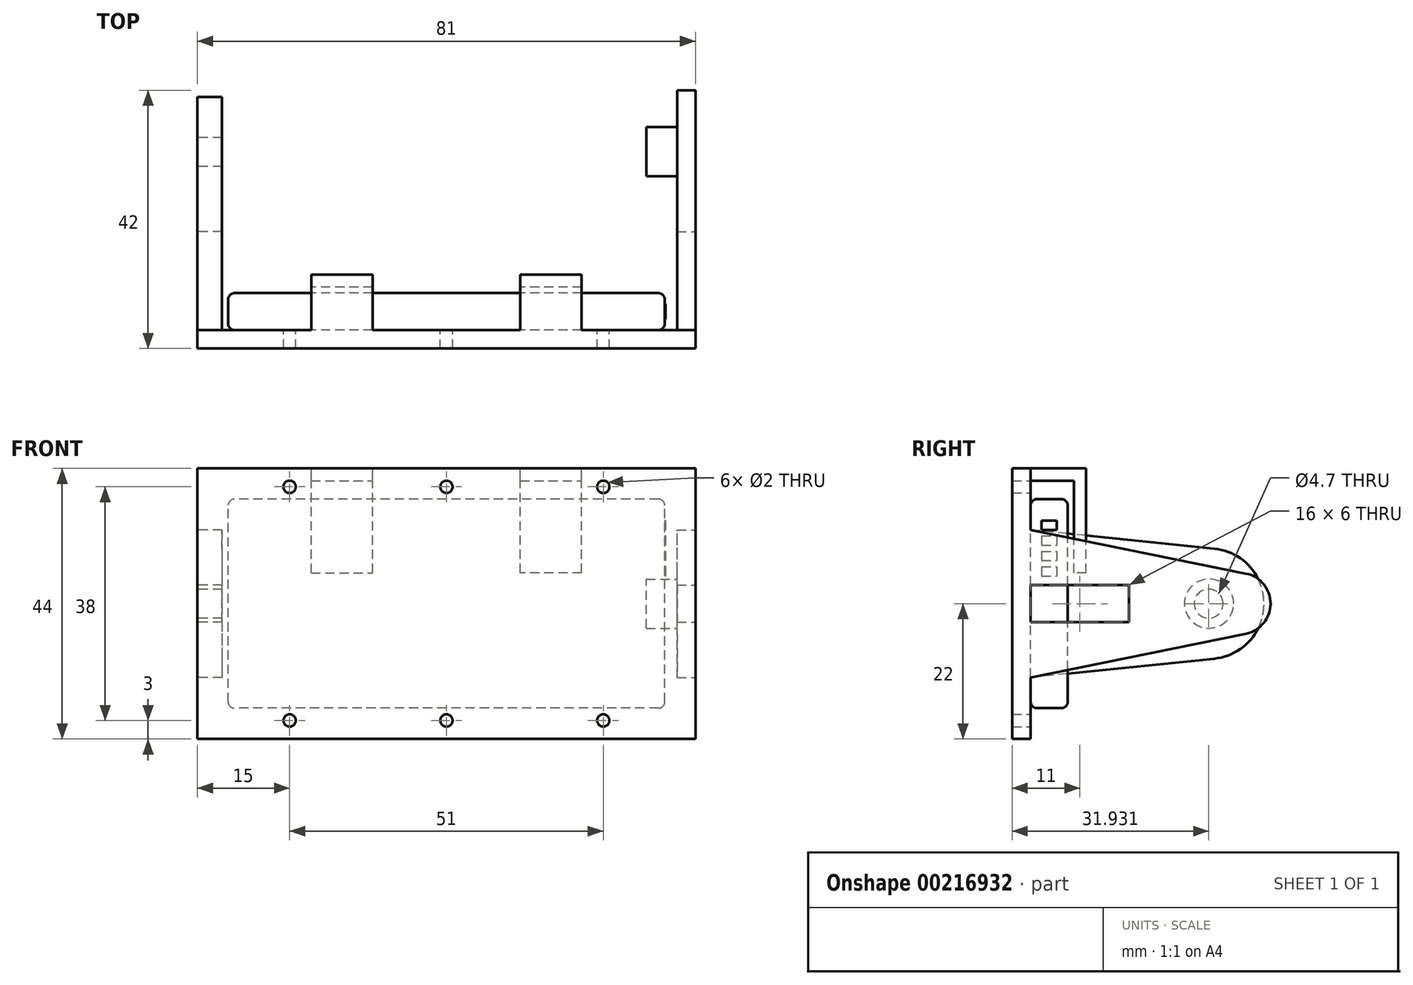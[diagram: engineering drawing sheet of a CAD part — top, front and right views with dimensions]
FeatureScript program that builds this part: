
annotation { "Feature Type Name" : "Feature", "Feature Type Description" : "" }
export const myFeature = defineFeature(function(context is Context, id is Id, definition is map)
    precondition{}
    {
        {
            var Q0;
            Q0=qCreatedBy(makeId("Front.planeOp"),FACE);
            var sketch = newSketch(context, id + "F0", { "sketchPlane" : qUnion([Q0])});
            skLineSegment(sketch, "E0.bottom", {"start": v(35.5, -17) * mm, "end": v(-35.5, -17) * mm});
            skLineSegment(sketch, "E0.top", {"start": v(35.5, 17) * mm, "end": v(-35.5, 17) * mm});
            skLineSegment(sketch, "E0.left", {"start": v(35.5, -17) * mm, "end": v(35.5, 17) * mm});
            skLineSegment(sketch, "E0.right", {"start": v(-35.5, -17) * mm, "end": v(-35.5, 17) * mm});
            skPoint(sketch, "E0.middle", {"position": v(0, 0) * mm});
            skSolve(sketch);
        }
        {
            var Q0;
            Q0 = qSketchRegion(id + "F0", true);
            extrude(context, id + "F1", {"entities" : qUnion([Q0]), "endBound" : BoundingType.SYMMETRIC, "depth" : 6 * mm});
        }
        {
            var Q0;
            Q0=makeQuery(id+"F1.opExtrude","CAP_EDGE",EDGE,{"disambiguationData":[OSD([sQuery(id+"F0.wireOp",EDGE,"E0.top")])],"isStart":false});
            var Q1;
            Q1=makeQuery(id+"F1.opExtrude","CAP_EDGE",EDGE,{"disambiguationData":[OSD([sQuery(id+"F0.wireOp",EDGE,"E0.top")])],"isStart":true});
            var Q2;
            Q2=makeQuery(id+"F1.opExtrude","CAP_EDGE",EDGE,{"disambiguationData":[OSD([sQuery(id+"F0.wireOp",EDGE,"E0.left")])],"isStart":false});
            var Q3;
            Q3=makeQuery(id+"F1.opExtrude","CAP_EDGE",EDGE,{"disambiguationData":[OSD([sQuery(id+"F0.wireOp",EDGE,"E0.left")])],"isStart":true});
            var Q4;
            Q4=makeQuery(id+"F1.opExtrude","CAP_EDGE",EDGE,{"disambiguationData":[OSD([sQuery(id+"F0.wireOp",EDGE,"E0.bottom")])],"isStart":false});
            var Q5;
            Q5=makeQuery(id+"F1.opExtrude","SWEPT_EDGE",EDGE,{"disambiguationData":[OSD([sQuery(id+"F0.wireOp",EDGE,"E0.bottom"),sQuery(id+"F0.wireOp",EDGE,"E0.left")])]});
            var Q6;
            Q6=makeQuery(id+"F1.opExtrude","SWEPT_EDGE",EDGE,{"disambiguationData":[OSD([sQuery(id+"F0.wireOp",EDGE,"E0.top"),sQuery(id+"F0.wireOp",EDGE,"E0.right")])]});
            var Q7;
            Q7=makeQuery(id+"F1.opExtrude","CAP_EDGE",EDGE,{"disambiguationData":[OSD([sQuery(id+"F0.wireOp",EDGE,"E0.right")])],"isStart":false});
            var Q8;
            Q8=makeQuery(id+"F1.opExtrude","CAP_EDGE",EDGE,{"disambiguationData":[OSD([sQuery(id+"F0.wireOp",EDGE,"E0.right")])],"isStart":true});
            var Q9;
            Q9=makeQuery(id+"F1.opExtrude","CAP_EDGE",EDGE,{"disambiguationData":[OSD([sQuery(id+"F0.wireOp",EDGE,"E0.bottom")])],"isStart":true});
            var Q10;
            Q10=makeQuery(id+"F1.opExtrude","SWEPT_EDGE",EDGE,{"disambiguationData":[OSD([sQuery(id+"F0.wireOp",EDGE,"E0.bottom"),sQuery(id+"F0.wireOp",EDGE,"E0.right")])]});
            var Q11;
            Q11=makeQuery(id+"F1.opExtrude","SWEPT_EDGE",EDGE,{"disambiguationData":[OSD([sQuery(id+"F0.wireOp",EDGE,"E0.top"),sQuery(id+"F0.wireOp",EDGE,"E0.left")])]});
            fillet(context, id + "F2", {"entities" : qUnion([Q0, Q1, Q2, Q3, Q4, Q5, Q6, Q7, Q8, Q9, Q10, Q11]), "radius" : 1 * mm, "tangentPropagation" : true, "allowEdgeOverflow" : false});
        }
        {
            var Q0;
            Q0=makeQuery(id+"F1.opExtrude","SWEPT_FACE",FACE,{"disambiguationData":[OSD([sQuery(id+"F0.wireOp",EDGE,"E0.left")])]});
            var sketch = newSketch(context, id + "F3", { "sketchPlane" : qUnion([Q0])});
            skLineSegment(sketch, "E1.bottom", {"start": v(-1.25, 13.5) * mm, "end": v(1.25, 13.5) * mm});
            skLineSegment(sketch, "E1.top", {"start": v(-1.25, 12) * mm, "end": v(1.25, 12) * mm});
            skLineSegment(sketch, "E1.left", {"start": v(-1.25, 13.5) * mm, "end": v(-1.25, 12) * mm});
            skLineSegment(sketch, "E1.right", {"start": v(1.25, 13.5) * mm, "end": v(1.25, 12) * mm});
            skLineSegment(sketch, "E2.bottom", {"start": v(-1.25, 11) * mm, "end": v(1.25, 11) * mm});
            skLineSegment(sketch, "E2.top", {"start": v(-1.25, 9.5) * mm, "end": v(1.25, 9.5) * mm});
            skLineSegment(sketch, "E2.left", {"start": v(-1.25, 11) * mm, "end": v(-1.25, 9.5) * mm});
            skLineSegment(sketch, "E2.right", {"start": v(1.25, 11) * mm, "end": v(1.25, 9.5) * mm});
            skLineSegment(sketch, "E3.bottom", {"start": v(-1.25, 8.5) * mm, "end": v(1.25, 8.5) * mm});
            skLineSegment(sketch, "E3.top", {"start": v(-1.25, 7) * mm, "end": v(1.25, 7) * mm});
            skLineSegment(sketch, "E3.left", {"start": v(-1.25, 8.5) * mm, "end": v(-1.25, 7) * mm});
            skLineSegment(sketch, "E3.right", {"start": v(1.25, 8.5) * mm, "end": v(1.25, 7) * mm});
            skLineSegment(sketch, "E4.bottom", {"start": v(-1.25, 6) * mm, "end": v(1.25, 6) * mm});
            skLineSegment(sketch, "E4.top", {"start": v(-1.25, 4.5) * mm, "end": v(1.25, 4.5) * mm});
            skLineSegment(sketch, "E4.left", {"start": v(-1.25, 6) * mm, "end": v(-1.25, 4.5) * mm});
            skLineSegment(sketch, "E4.right", {"start": v(1.25, 6) * mm, "end": v(1.25, 4.5) * mm});
            skSolve(sketch);
        }
        {
            var Q0;
            Q0 = qSketchRegion(id + "F3", true);
            extrude(context, id + "F4", {"entities" : qUnion([Q0]), "operationType" : NewBodyOperationType.ADD, "depth" : 0.1 * mm});
        }
        {
            var Q0;
            Q0=makeQuery(id+"F1.opExtrude","CAP_FACE",FACE,{"disambiguationData":[OSD([sQuery(id+"F0.wireOp",EDGE,"E0.bottom"),sQuery(id+"F0.wireOp",EDGE,"E0.top"),sQuery(id+"F0.wireOp",EDGE,"E0.left"),sQuery(id+"F0.wireOp",EDGE,"E0.right")])],"isStart":false});
            var sketch = newSketch(context, id + "F5", { "sketchPlane" : qUnion([Q0])});
            skLineSegment(sketch, "E5.0", {"start": v(40.5, 22) * mm, "end": v(-40.5, 22) * mm});
            skLineSegment(sketch, "E5.1", {"start": v(40.5, -22) * mm, "end": v(40.5, 22) * mm});
            skLineSegment(sketch, "E5.2", {"start": v(-40.5, -22) * mm, "end": v(40.5, -22) * mm});
            skLineSegment(sketch, "E5.3", {"start": v(-40.5, 22) * mm, "end": v(-40.5, -22) * mm});
            skSolve(sketch);
        }
        {
            var Q0;
            Q0 = qSketchRegion(id + "F5", true);
            extrude(context, id + "F6", {"entities" : qUnion([Q0]), "depth" : 3 * mm});
        }
        {
            var Q0;
            Q0=makeQuery(id+"F6.opExtrude","SWEPT_FACE",FACE,{"disambiguationData":[OSD([sQuery(id+"F5.wireOp",EDGE,"E5.3")])]});
            var sketch = newSketch(context, id + "F7", { "sketchPlane" : qUnion([Q0])});
            skCircle(sketch, "E6", {"center": v(-25.93, 0) * mm, "radius": 9 * mm});
            skLineSegment(sketch, "E7", {"start": v(-26.84, -8.95) * mm, "end": v(3, -12) * mm});
            skLineSegment(sketch, "E8", {"start": v(-26.84, 8.95) * mm, "end": v(3, 12) * mm});
            skLineSegment(sketch, "E9", {"start": v(3, 12) * mm, "end": v(3, 3) * mm});
            skLineSegment(sketch, "E10.bottom", {"start": v(-13, -3) * mm, "end": v(3, -3) * mm});
            skLineSegment(sketch, "E10.top", {"start": v(-13, 3) * mm, "end": v(3, 3) * mm});
            skLineSegment(sketch, "E10.left", {"start": v(-13, -3) * mm, "end": v(-13, 3) * mm});
            skLineSegment(sketch, "E11.trimOffspring", {"start": v(3, -3) * mm, "end": v(3, -12) * mm});
            skCircle(sketch, "E12", {"center": v(-25.93, 0) * mm, "radius": 2.35 * mm});
            skSolve(sketch);
        }
        {
            var Q0;
            Q0 = qSketchRegion(id + "F7", true);
            extrude(context, id + "F8", {"entities" : qUnion([Q0]), "operationType" : NewBodyOperationType.ADD, "oppositeDirection" : true, "depth" : 4 * mm});
        }
        {
            var Q0;
            Q0=makeQuery(id+"F6.opExtrude","SWEPT_FACE",FACE,{"disambiguationData":[OSD([sQuery(id+"F5.wireOp",EDGE,"E5.1")])]});
            var sketch = newSketch(context, id + "F9", { "sketchPlane" : qUnion([Q0])});
            skCircle(sketch, "E13", {"center": v(31, 0) * mm, "radius": 5 * mm});
            skLineSegment(sketch, "E14", {"start": v(32, 4.9) * mm, "end": v(-3, 12) * mm});
            skLineSegment(sketch, "E15", {"start": v(32, -4.9) * mm, "end": v(-3, -12) * mm});
            skLineSegment(sketch, "E16", {"start": v(-3, -12) * mm, "end": v(-3, -3) * mm});
            skLineSegment(sketch, "E17.bottom", {"start": v(-3, 3) * mm, "end": v(13, 3) * mm});
            skLineSegment(sketch, "E17.top", {"start": v(-3, -3) * mm, "end": v(13, -3) * mm});
            skLineSegment(sketch, "E17.right", {"start": v(13, 3) * mm, "end": v(13, -3) * mm});
            skLineSegment(sketch, "E18.trimOffspring", {"start": v(-3, 3) * mm, "end": v(-3, 12) * mm});
            skSolve(sketch);
        }
        {
            var Q0;
            Q0 = qSketchRegion(id + "F9", true);
            extrude(context, id + "F10", {"entities" : qUnion([Q0]), "operationType" : NewBodyOperationType.ADD, "oppositeDirection" : true, "depth" : 3 * mm});
        }
        {
            var Q0;
            Q0=makeQuery(id+"F10.boolean.opBoolean","MERGE",FACE,{"derivedFrom":[makeQuery(id+"F6.opExtrude","SWEPT_FACE",FACE,{"disambiguationData":[OSD([sQuery(id+"F5.wireOp",EDGE,"E5.1")])]}),makeQuery(id+"F10.opExtrude","CAP_FACE",FACE,{"disambiguationData":[OSD([sQuery(id+"F9.wireOp",EDGE,"E13"),sQuery(id+"F9.wireOp",EDGE,"E14"),sQuery(id+"F9.wireOp",EDGE,"E15"),sQuery(id+"F9.wireOp",EDGE,"E16"),sQuery(id+"F9.wireOp",EDGE,"E17.bottom"),sQuery(id+"F9.wireOp",EDGE,"E17.top"),sQuery(id+"F9.wireOp",EDGE,"E17.right"),sQuery(id+"F9.wireOp",EDGE,"E18.trimOffspring")])],"isStart":true})]});
            var sketch = newSketch(context, id + "F11", { "sketchPlane" : qUnion([Q0])});
            skCircle(sketch, "E19", {"center": v(26, 0) * mm, "radius": 4 * mm});
            skSolve(sketch);
        }
        {
            var Q0;
            Q0 = qSketchRegion(id + "F11", true);
            extrude(context, id + "F12", {"entities" : qUnion([Q0]), "operationType" : NewBodyOperationType.ADD, "oppositeDirection" : true, "depth" : 8 * mm});
        }
        {
            var Q0;
            Q0=makeQuery(id+"F6.opExtrude","CAP_FACE",FACE,{"disambiguationData":[OSD([sQuery(id+"F5.wireOp",EDGE,"E5.0"),sQuery(id+"F5.wireOp",EDGE,"E5.1"),sQuery(id+"F5.wireOp",EDGE,"E5.2"),sQuery(id+"F5.wireOp",EDGE,"E5.3")])],"isStart":true});
            var sketch = newSketch(context, id + "F13", { "sketchPlane" : qUnion([Q0])});
            skLineSegment(sketch, "E20.bottom", {"start": v(22, 20) * mm, "end": v(12, 20) * mm});
            skLineSegment(sketch, "E20.top", {"start": v(22, 22) * mm, "end": v(12, 22) * mm});
            skLineSegment(sketch, "E20.left", {"start": v(22, 20) * mm, "end": v(22, 22) * mm});
            skLineSegment(sketch, "E20.right", {"start": v(12, 20) * mm, "end": v(12, 22) * mm});
            skLineSegment(sketch, "E21.bottom", {"start": v(-12, 20) * mm, "end": v(-22, 20) * mm});
            skLineSegment(sketch, "E21.top", {"start": v(-12, 22) * mm, "end": v(-22, 22) * mm});
            skLineSegment(sketch, "E21.left", {"start": v(-12, 20) * mm, "end": v(-12, 22) * mm});
            skLineSegment(sketch, "E21.right", {"start": v(-22, 20) * mm, "end": v(-22, 22) * mm});
            skSolve(sketch);
        }
        {
            var Q0;
            Q0 = qSketchRegion(id + "F13", true);
            extrude(context, id + "F14", {"entities" : qUnion([Q0]), "operationType" : NewBodyOperationType.ADD, "depth" : 9 * mm});
        }
        {
            var Q0;
            Q0=makeQuery(id+"F14.opExtrude","SWEPT_FACE",FACE,{"disambiguationData":[OSD([sQuery(id+"F13.wireOp",EDGE,"E20.bottom")])]});
            var sketch = newSketch(context, id + "F15", { "sketchPlane" : qUnion([Q0])});
            skLineSegment(sketch, "E22.bottom", {"start": v(-12, -6) * mm, "end": v(-22, -6) * mm});
            skLineSegment(sketch, "E22.top", {"start": v(-12, -4) * mm, "end": v(-22, -4) * mm});
            skLineSegment(sketch, "E22.left", {"start": v(-12, -6) * mm, "end": v(-12, -4) * mm});
            skLineSegment(sketch, "E22.right", {"start": v(-22, -6) * mm, "end": v(-22, -4) * mm});
            skLineSegment(sketch, "E23.bottom", {"start": v(22, -6) * mm, "end": v(12, -6) * mm});
            skLineSegment(sketch, "E23.top", {"start": v(22, -4) * mm, "end": v(12, -4) * mm});
            skLineSegment(sketch, "E23.left", {"start": v(22, -6) * mm, "end": v(22, -4) * mm});
            skLineSegment(sketch, "E23.right", {"start": v(12, -6) * mm, "end": v(12, -4) * mm});
            skSolve(sketch);
        }
        {
            var Q0;
            Q0 = qSketchRegion(id + "F15", true);
            extrude(context, id + "F16", {"entities" : qUnion([Q0]), "operationType" : NewBodyOperationType.ADD, "depth" : 15 * mm});
        }
        {
            var Q0;
            Q0=makeQuery(id+"F6.opExtrude","CAP_FACE",FACE,{"disambiguationData":[OSD([sQuery(id+"F5.wireOp",EDGE,"E5.0"),sQuery(id+"F5.wireOp",EDGE,"E5.1"),sQuery(id+"F5.wireOp",EDGE,"E5.2"),sQuery(id+"F5.wireOp",EDGE,"E5.3")])],"isStart":true});
            var sketch = newSketch(context, id + "F17", { "sketchPlane" : qUnion([Q0])});
            skCircle(sketch, "E24", {"center": v(25.5, 19) * mm, "radius": 1 * mm});
            skCircle(sketch, "E25", {"center": v(25.5, -19) * mm, "radius": 1 * mm});
            skCircle(sketch, "E26", {"center": v(-25.5, 19) * mm, "radius": 1 * mm});
            skCircle(sketch, "E27", {"center": v(-25.5, -19) * mm, "radius": 1 * mm});
            skCircle(sketch, "E28", {"center": v(0, -19) * mm, "radius": 1 * mm});
            skCircle(sketch, "E29", {"center": v(0, 19) * mm, "radius": 1 * mm});
            skSolve(sketch);
        }
        {
            var Q0;
            Q0 = qSketchRegion(id + "F17", true);
            extrude(context, id + "F18", {"entities" : qUnion([Q0]), "operationType" : NewBodyOperationType.REMOVE, "oppositeDirection" : true, "depth" : 25 * mm});
        }
    });
